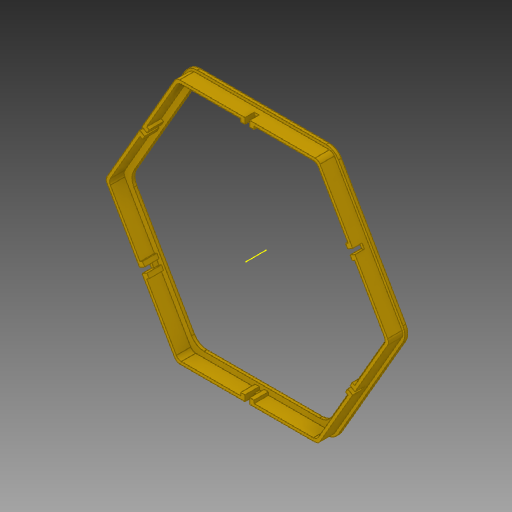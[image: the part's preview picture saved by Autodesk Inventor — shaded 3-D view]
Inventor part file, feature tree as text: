
AUTODESK INVENTOR PART (.ipt)
format: ipt  version: 2019 (Build 230136000, 136)  size: 279,552 bytes
history: native  units: mm
features: extrude x5, sketch x5, projected_geometry x3, fillet x2, other x1, pattern_circular x1
ambient origin geometry x8: Origin, YZ Plane, XZ Plane, XY Plane, X Axis, Y Axis, Z Axis, Center Point
bodies: Solid1 (feature_tree)
feature tree (17):
  extrude  "Extrusion1"  Depth=2.0mm
  extrude  "Extrusion5"  Depth=2.0mm
  extrude  "Extrusion6"  Depth=10.0mm
  fillet  "Fillet1"  [1 undecoded]
  fillet  "Fillet2"  Radius=4.0mm
  extrude  "Extrusion7"  TaperAngle=0.0deg  [1 undecoded]
  extrude  "Extrusion8"  Depth=4.0mm
  other  "Work Axis2"
  pattern_circular  "Circular Pattern1"  [2 undecoded]
  sketch  "Sketch1"  dims[d0=175.0mm d1=2.0mm]
  sketch  "Sketch5"  dims[d2=0.0mm d15=2.0mm]
  projected_geometry  "Projected Loop4"
  sketch  "Sketch7"  dims[d16=2.0mm d17=10.0mm d18=0.0mm d19=4.0mm]
  projected_geometry  "Projected Loop6"
  sketch  "Sketch8"  dims[d20=7.0mm d21=0.0mm]
  sketch  "Sketch9"  dims[d22=10.0mm d23=4.0mm d24=10.0mm d25=3.3mm d26=6.5mm d27=0.0mm d28=4.0mm d29=3.0mm d30=5.0mm d31=0.0mm d32=60.0mm d33=360.0deg]
  projected_geometry  "Projected Loop7"
note: 4 required parameter values undecoded (feature->parameter linkage not recoverable at this tier; creation-order binding heuristic only, values carry confidence <= 0.55)
